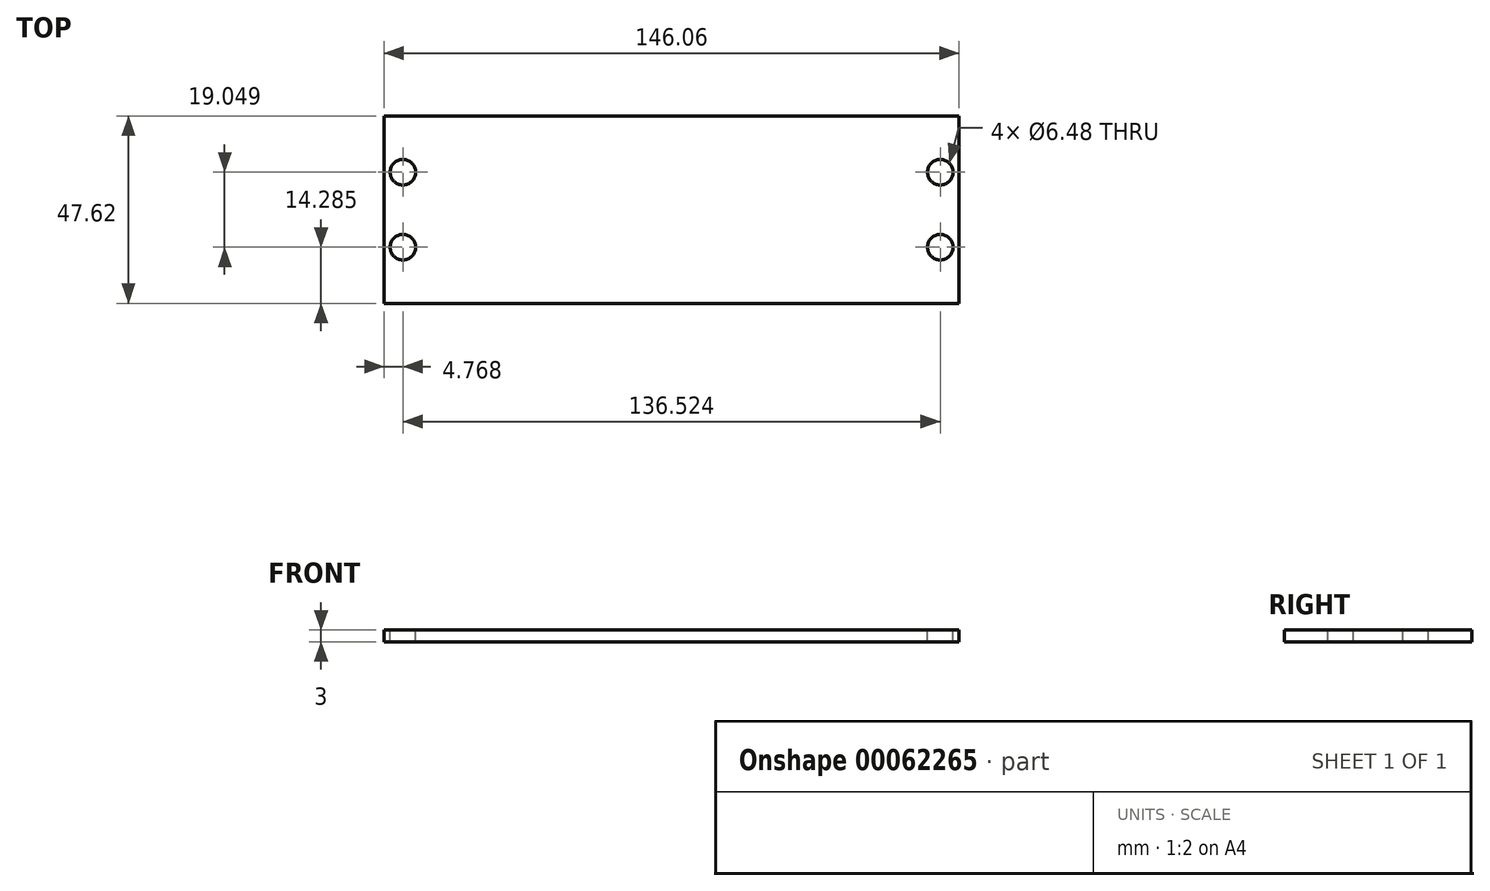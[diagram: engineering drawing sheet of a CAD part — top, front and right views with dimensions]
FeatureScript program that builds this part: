
annotation { "Feature Type Name" : "Feature", "Feature Type Description" : "" }
export const myFeature = defineFeature(function(context is Context, id is Id, definition is map)
    precondition{}
    {
        {
            var Q0;
            Q0=qCreatedBy(makeId("Top.planeOp"),FACE);
            var sketch = newSketch(context, id + "F0", { "sketchPlane" : qUnion([Q0])});
            skLineSegment(sketch, "E0", {"start": v(72.22, -23.01) * mm, "end": v(72.22, -15.86) * mm});
            skLineSegment(sketch, "E1", {"start": v(72.22, -3.19) * mm, "end": v(72.22, 3.17) * mm});
            skLineSegment(sketch, "E2", {"start": v(-68.2, -15.87) * mm, "end": v(-72.23, -15.87) * mm});
            skLineSegment(sketch, "E3", {"start": v(-68.26, 15.87) * mm, "end": v(-72.23, 15.87) * mm});
            skLineSegment(sketch, "E4", {"start": v(68.26, 15.87) * mm, "end": v(72.22, 15.87) * mm});
            skLineSegment(sketch, "E5", {"start": v(-68.26, 3.17) * mm, "end": v(-72.23, 3.17) * mm});
            skLineSegment(sketch, "E6", {"start": v(68.26, 3.17) * mm, "end": v(72.22, 3.17) * mm});
            skLineSegment(sketch, "E7", {"start": v(67.83, -3.19) * mm, "end": v(72.22, -3.19) * mm});
            skArc(sketch, "E8", {"start": v(67.83, -3.19) * mm, "mid": v(61.93, -9.96) * mm, "end": v(68.7, -15.86) * mm});
            skLineSegment(sketch, "E9", {"start": v(68.7, -15.86) * mm, "end": v(72.22, -15.86) * mm});
            skLineSegment(sketch, "E10", {"start": v(-68.33, -3.17) * mm, "end": v(-72.23, -3.17) * mm});
            skArc(sketch, "E11", {"start": v(68.26, 15.87) * mm, "mid": v(61.91, 9.52) * mm, "end": v(68.26, 3.17) * mm});
            skLineSegment(sketch, "E12", {"start": v(72.22, 15.87) * mm, "end": v(72.22, 23.01) * mm});
            skLineSegment(sketch, "E13", {"start": v(-72.23, -3.17) * mm, "end": v(-72.23, 3.17) * mm});
            skLineSegment(sketch, "E14", {"start": v(-72.23, 15.87) * mm, "end": v(-72.23, 23.01) * mm});
            skLineSegment(sketch, "E15", {"start": v(72.22, -23.01) * mm, "end": v(-72.23, -23.01) * mm});
            skArc(sketch, "E16", {"start": v(-68.26, 3.17) * mm, "mid": v(-61.91, 9.52) * mm, "end": v(-68.26, 15.87) * mm});
            skLineSegment(sketch, "E17", {"start": v(-72.23, 23.01) * mm, "end": v(72.23, 23.01) * mm});
            skArc(sketch, "E18", {"start": v(-68.2, -15.87) * mm, "mid": v(-61.91, -9.46) * mm, "end": v(-68.33, -3.17) * mm});
            skLineSegment(sketch, "E19", {"start": v(-72.23, -23.01) * mm, "end": v(-72.23, -15.87) * mm});
            skCircle(sketch, "E20", {"center": v(68.26, -9.52) * mm, "radius": 3.24 * mm});
            skCircle(sketch, "E21", {"center": v(-68.26, 9.52) * mm, "radius": 3.24 * mm});
            skLineSegment(sketch, "E22", {"start": v(-73.03, -23.81) * mm, "end": v(-73.03, 23.81) * mm});
            skCircle(sketch, "E23", {"center": v(-68.26, -9.52) * mm, "radius": 3.24 * mm});
            skLineSegment(sketch, "E24", {"start": v(73.03, -23.81) * mm, "end": v(73.03, 23.81) * mm});
            skLineSegment(sketch, "E25", {"start": v(-73.03, 23.81) * mm, "end": v(73.03, 23.81) * mm});
            skLineSegment(sketch, "E26", {"start": v(73.03, -23.81) * mm, "end": v(-73.03, -23.81) * mm});
            skCircle(sketch, "E27", {"center": v(68.26, 9.52) * mm, "radius": 3.24 * mm});
            skSolve(sketch);
        }
        {
            var Q0;
            Q0 = qSketchRegion(id + "F0", true);
            var Q1;
            Q1=makeQuery(id+"F0.imprint","IMPRINT",FACE,{"disambiguationData":[TD([[makeQuery(id+"F0.imprint","IMPRINT",EDGE,{"derivedFrom":sQuery(id+"F0.wireOp",EDGE,"E0")}),1.0]])]});
            extrude(context, id + "F1", {"entities" : qUnion([Q0, Q1]), "oppositeDirection" : true, "depth" : 3 * mm, "offsetDistance" : 25 * mm});
        }
    });
